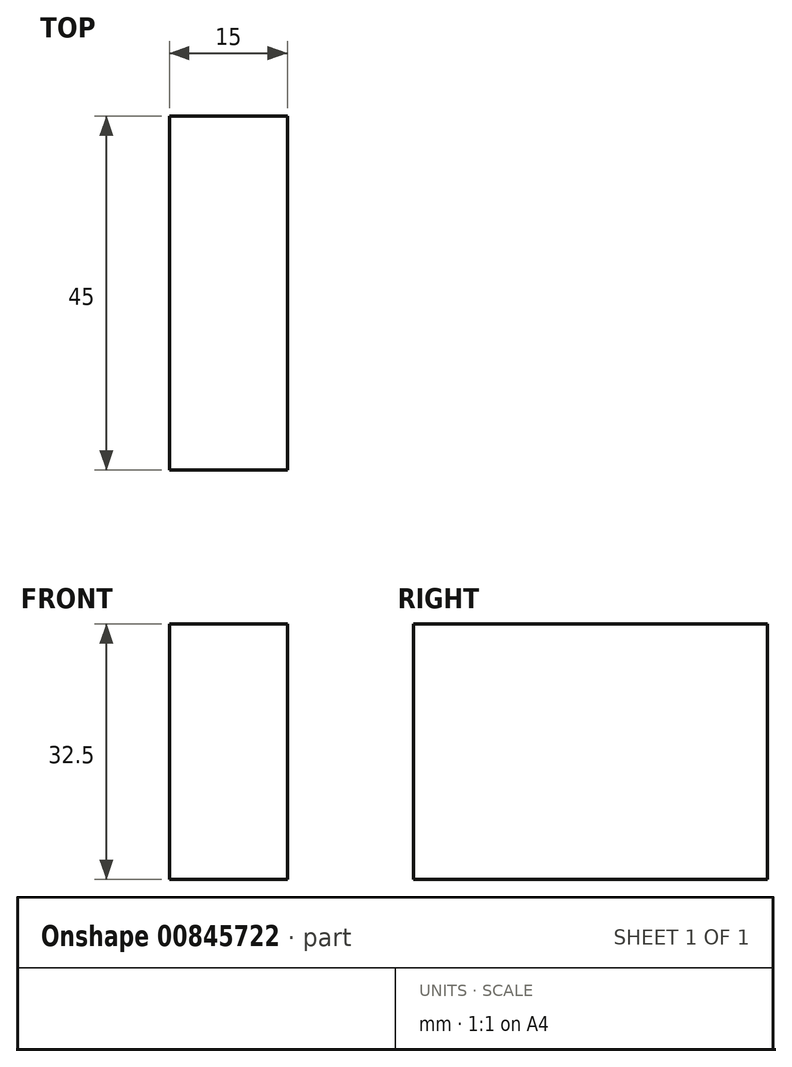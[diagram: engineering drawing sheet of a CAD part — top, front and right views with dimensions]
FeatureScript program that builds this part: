
annotation { "Feature Type Name" : "Feature", "Feature Type Description" : "" }
export const myFeature = defineFeature(function(context is Context, id is Id, definition is map)
    precondition{}
    {
        {
            var Q0;
            Q0=qCreatedBy(makeId("Right.planeOp"),FACE);
            var sketch = newSketch(context, id + "F0", { "sketchPlane" : qUnion([Q0])});
            skLineSegment(sketch, "E0", {"start": v(0, 0) * mm, "end": v(0, 32.5) * mm});
            skLineSegment(sketch, "E1", {"start": v(0, 0) * mm, "end": v(-5, 0) * mm});
            skLineSegment(sketch, "E2", {"start": v(-5, 0) * mm, "end": v(-45, 0) * mm});
            skLineSegment(sketch, "E3", {"start": v(-45, 0) * mm, "end": v(-45, 32.5) * mm});
            skLineSegment(sketch, "E4", {"start": v(-45, 32.5) * mm, "end": v(0, 32.5) * mm});
            skSolve(sketch);
        }
        {
            var Q0;
            Q0=makeQuery(id+"F0.imprint","IMPRINT",FACE,{"disambiguationData":[TD([[makeQuery(id+"F0.imprint","IMPRINT",EDGE,{"derivedFrom":sQuery(id+"F0.wireOp",EDGE,"E0")}),1.0]])]});
            extrude(context, id + "F1", {"entities" : qUnion([Q0]), "depth" : 15 * mm, "offsetDistance" : 25 * mm});
        }
    });
